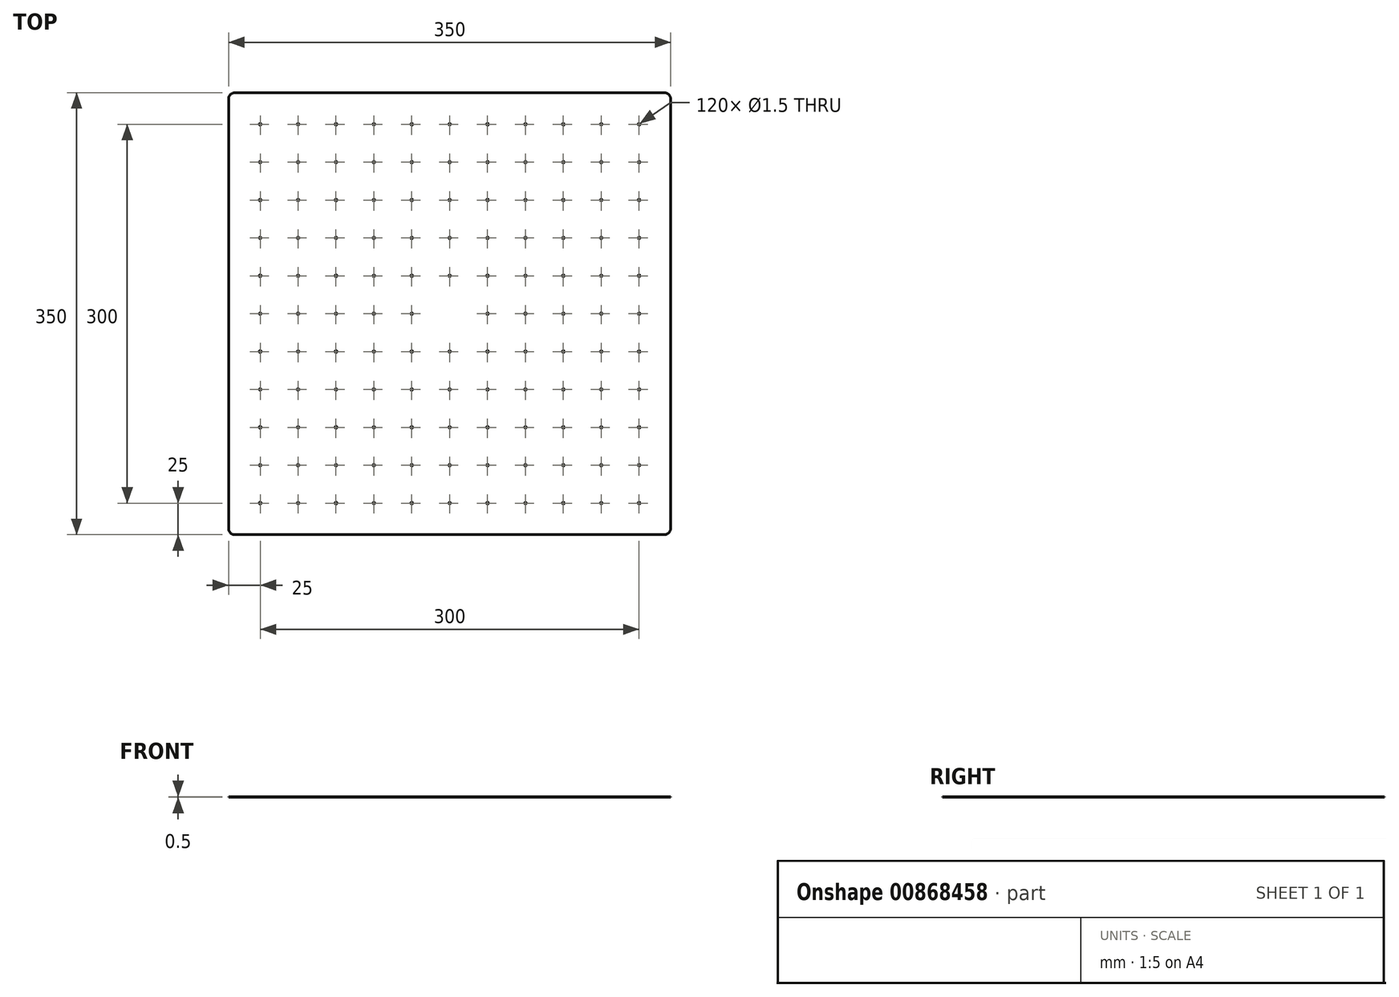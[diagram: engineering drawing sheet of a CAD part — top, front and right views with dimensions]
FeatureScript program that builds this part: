
annotation { "Feature Type Name" : "Feature", "Feature Type Description" : "" }
export const myFeature = defineFeature(function(context is Context, id is Id, definition is map)
    precondition{}
    {
        {
            var Q0;
            Q0=qCreatedBy(makeId("Top.planeOp"),FACE);
            var sketch = newSketch(context, id + "F0", { "sketchPlane" : qUnion([Q0])});
            skLineSegment(sketch, "E0.bottom", {"start": v(-170, -175) * mm, "end": v(170, -175) * mm});
            skLineSegment(sketch, "E0.top", {"start": v(-170, 175) * mm, "end": v(170, 175) * mm});
            skLineSegment(sketch, "E0.left", {"start": v(-175, -170) * mm, "end": v(-175, 170) * mm});
            skLineSegment(sketch, "E0.right", {"start": v(175, -170) * mm, "end": v(175, 170) * mm});
            skPoint(sketch, "E0.middle", {"position": v(0, 0) * mm});
            skPoint(sketch, "E1.visualSharp", {"position": v(-175, 175) * mm});
            skArc(sketch, "E1.filletArc", {"start": v(-170, 175) * mm, "mid": v(-173.54, 173.54) * mm, "end": v(-175, 170) * mm});
            skPoint(sketch, "E2.visualSharp", {"position": v(175, 175) * mm});
            skArc(sketch, "E2.filletArc", {"start": v(175, 170) * mm, "mid": v(173.54, 173.54) * mm, "end": v(170, 175) * mm});
            skPoint(sketch, "E3.visualSharp", {"position": v(175, -175) * mm});
            skArc(sketch, "E3.filletArc", {"start": v(170, -175) * mm, "mid": v(173.54, -173.54) * mm, "end": v(175, -170) * mm});
            skPoint(sketch, "E4.visualSharp", {"position": v(-175, -175) * mm});
            skArc(sketch, "E4.filletArc", {"start": v(-175, -170) * mm, "mid": v(-173.54, -173.54) * mm, "end": v(-170, -175) * mm});
            skCircle(sketch, "E5", {"center": v(-150, 150) * mm, "radius": 0.75 * mm});
            skCircle(sketch, "E6.0.1.0", {"center": v(-150, 120) * mm, "radius": 0.75 * mm});
            skCircle(sketch, "E6.0.2.0", {"center": v(-150, 90) * mm, "radius": 0.75 * mm});
            skCircle(sketch, "E6.0.3.0", {"center": v(-150, 60) * mm, "radius": 0.75 * mm});
            skCircle(sketch, "E6.0.4.0", {"center": v(-150, 30) * mm, "radius": 0.75 * mm});
            skCircle(sketch, "E6.0.5.0", {"center": v(-150, 0) * mm, "radius": 0.75 * mm});
            skCircle(sketch, "E6.0.6.0", {"center": v(-150, -30) * mm, "radius": 0.75 * mm});
            skCircle(sketch, "E6.0.7.0", {"center": v(-150, -60) * mm, "radius": 0.75 * mm});
            skCircle(sketch, "E6.0.8.0", {"center": v(-150, -90) * mm, "radius": 0.75 * mm});
            skCircle(sketch, "E6.0.9.0", {"center": v(-150, -120) * mm, "radius": 0.75 * mm});
            skCircle(sketch, "E6.0.10.0", {"center": v(-150, -150) * mm, "radius": 0.75 * mm});
            skCircle(sketch, "E6.1.0.0", {"center": v(-120, 150) * mm, "radius": 0.75 * mm});
            skCircle(sketch, "E6.1.1.0", {"center": v(-120, 120) * mm, "radius": 0.75 * mm});
            skCircle(sketch, "E6.1.2.0", {"center": v(-120, 90) * mm, "radius": 0.75 * mm});
            skCircle(sketch, "E6.1.3.0", {"center": v(-120, 60) * mm, "radius": 0.75 * mm});
            skCircle(sketch, "E6.1.4.0", {"center": v(-120, 30) * mm, "radius": 0.75 * mm});
            skCircle(sketch, "E6.1.5.0", {"center": v(-120, 0) * mm, "radius": 0.75 * mm});
            skCircle(sketch, "E6.1.6.0", {"center": v(-120, -30) * mm, "radius": 0.75 * mm});
            skCircle(sketch, "E6.1.7.0", {"center": v(-120, -60) * mm, "radius": 0.75 * mm});
            skCircle(sketch, "E6.1.8.0", {"center": v(-120, -90) * mm, "radius": 0.75 * mm});
            skCircle(sketch, "E6.1.9.0", {"center": v(-120, -120) * mm, "radius": 0.75 * mm});
            skCircle(sketch, "E6.1.10.0", {"center": v(-120, -150) * mm, "radius": 0.75 * mm});
            skCircle(sketch, "E6.2.0.0", {"center": v(-90, 150) * mm, "radius": 0.75 * mm});
            skCircle(sketch, "E6.2.1.0", {"center": v(-90, 120) * mm, "radius": 0.75 * mm});
            skCircle(sketch, "E6.2.2.0", {"center": v(-90, 90) * mm, "radius": 0.75 * mm});
            skCircle(sketch, "E6.2.3.0", {"center": v(-90, 60) * mm, "radius": 0.75 * mm});
            skCircle(sketch, "E6.2.4.0", {"center": v(-90, 30) * mm, "radius": 0.75 * mm});
            skCircle(sketch, "E6.2.5.0", {"center": v(-90, 0) * mm, "radius": 0.75 * mm});
            skCircle(sketch, "E6.2.6.0", {"center": v(-90, -30) * mm, "radius": 0.75 * mm});
            skCircle(sketch, "E6.2.7.0", {"center": v(-90, -60) * mm, "radius": 0.75 * mm});
            skCircle(sketch, "E6.2.8.0", {"center": v(-90, -90) * mm, "radius": 0.75 * mm});
            skCircle(sketch, "E6.2.9.0", {"center": v(-90, -120) * mm, "radius": 0.75 * mm});
            skCircle(sketch, "E6.2.10.0", {"center": v(-90, -150) * mm, "radius": 0.75 * mm});
            skCircle(sketch, "E6.3.0.0", {"center": v(-60, 150) * mm, "radius": 0.75 * mm});
            skCircle(sketch, "E6.3.1.0", {"center": v(-60, 120) * mm, "radius": 0.75 * mm});
            skCircle(sketch, "E6.3.2.0", {"center": v(-60, 90) * mm, "radius": 0.75 * mm});
            skCircle(sketch, "E6.3.3.0", {"center": v(-60, 60) * mm, "radius": 0.75 * mm});
            skCircle(sketch, "E6.3.4.0", {"center": v(-60, 30) * mm, "radius": 0.75 * mm});
            skCircle(sketch, "E6.3.5.0", {"center": v(-60, 0) * mm, "radius": 0.75 * mm});
            skCircle(sketch, "E6.3.6.0", {"center": v(-60, -30) * mm, "radius": 0.75 * mm});
            skCircle(sketch, "E6.3.7.0", {"center": v(-60, -60) * mm, "radius": 0.75 * mm});
            skCircle(sketch, "E6.3.8.0", {"center": v(-60, -90) * mm, "radius": 0.75 * mm});
            skCircle(sketch, "E6.3.9.0", {"center": v(-60, -120) * mm, "radius": 0.75 * mm});
            skCircle(sketch, "E6.3.10.0", {"center": v(-60, -150) * mm, "radius": 0.75 * mm});
            skCircle(sketch, "E6.4.0.0", {"center": v(-30, 150) * mm, "radius": 0.75 * mm});
            skCircle(sketch, "E6.4.1.0", {"center": v(-30, 120) * mm, "radius": 0.75 * mm});
            skCircle(sketch, "E6.4.2.0", {"center": v(-30, 90) * mm, "radius": 0.75 * mm});
            skCircle(sketch, "E6.4.3.0", {"center": v(-30, 60) * mm, "radius": 0.75 * mm});
            skCircle(sketch, "E6.4.4.0", {"center": v(-30, 30) * mm, "radius": 0.75 * mm});
            skCircle(sketch, "E6.4.5.0", {"center": v(-30, 0) * mm, "radius": 0.75 * mm});
            skCircle(sketch, "E6.4.6.0", {"center": v(-30, -30) * mm, "radius": 0.75 * mm});
            skCircle(sketch, "E6.4.7.0", {"center": v(-30, -60) * mm, "radius": 0.75 * mm});
            skCircle(sketch, "E6.4.8.0", {"center": v(-30, -90) * mm, "radius": 0.75 * mm});
            skCircle(sketch, "E6.4.9.0", {"center": v(-30, -120) * mm, "radius": 0.75 * mm});
            skCircle(sketch, "E6.4.10.0", {"center": v(-30, -150) * mm, "radius": 0.75 * mm});
            skCircle(sketch, "E6.5.0.0", {"center": v(0, 150) * mm, "radius": 0.75 * mm});
            skCircle(sketch, "E6.5.1.0", {"center": v(0, 120) * mm, "radius": 0.75 * mm});
            skCircle(sketch, "E6.5.2.0", {"center": v(0, 90) * mm, "radius": 0.75 * mm});
            skCircle(sketch, "E6.5.3.0", {"center": v(0, 60) * mm, "radius": 0.75 * mm});
            skCircle(sketch, "E6.5.4.0", {"center": v(0, 30) * mm, "radius": 0.75 * mm});
            skCircle(sketch, "E6.5.5.0", {"center": v(0, 0) * mm, "radius": 0.75 * mm});
            skCircle(sketch, "E6.5.6.0", {"center": v(0, -30) * mm, "radius": 0.75 * mm});
            skCircle(sketch, "E6.5.7.0", {"center": v(0, -60) * mm, "radius": 0.75 * mm});
            skCircle(sketch, "E6.5.8.0", {"center": v(0, -90) * mm, "radius": 0.75 * mm});
            skCircle(sketch, "E6.5.9.0", {"center": v(0, -120) * mm, "radius": 0.75 * mm});
            skCircle(sketch, "E6.5.10.0", {"center": v(0, -150) * mm, "radius": 0.75 * mm});
            skCircle(sketch, "E6.6.0.0", {"center": v(30, 150) * mm, "radius": 0.75 * mm});
            skCircle(sketch, "E6.6.1.0", {"center": v(30, 120) * mm, "radius": 0.75 * mm});
            skCircle(sketch, "E6.6.2.0", {"center": v(30, 90) * mm, "radius": 0.75 * mm});
            skCircle(sketch, "E6.6.3.0", {"center": v(30, 60) * mm, "radius": 0.75 * mm});
            skCircle(sketch, "E6.6.4.0", {"center": v(30, 30) * mm, "radius": 0.75 * mm});
            skCircle(sketch, "E6.6.5.0", {"center": v(30, 0) * mm, "radius": 0.75 * mm});
            skCircle(sketch, "E6.6.6.0", {"center": v(30, -30) * mm, "radius": 0.75 * mm});
            skCircle(sketch, "E6.6.7.0", {"center": v(30, -60) * mm, "radius": 0.75 * mm});
            skCircle(sketch, "E6.6.8.0", {"center": v(30, -90) * mm, "radius": 0.75 * mm});
            skCircle(sketch, "E6.6.9.0", {"center": v(30, -120) * mm, "radius": 0.75 * mm});
            skCircle(sketch, "E6.6.10.0", {"center": v(30, -150) * mm, "radius": 0.75 * mm});
            skCircle(sketch, "E6.7.0.0", {"center": v(60, 150) * mm, "radius": 0.75 * mm});
            skCircle(sketch, "E6.7.1.0", {"center": v(60, 120) * mm, "radius": 0.75 * mm});
            skCircle(sketch, "E6.7.2.0", {"center": v(60, 90) * mm, "radius": 0.75 * mm});
            skCircle(sketch, "E6.7.3.0", {"center": v(60, 60) * mm, "radius": 0.75 * mm});
            skCircle(sketch, "E6.7.4.0", {"center": v(60, 30) * mm, "radius": 0.75 * mm});
            skCircle(sketch, "E6.7.5.0", {"center": v(60, 0) * mm, "radius": 0.75 * mm});
            skCircle(sketch, "E6.7.6.0", {"center": v(60, -30) * mm, "radius": 0.75 * mm});
            skCircle(sketch, "E6.7.7.0", {"center": v(60, -60) * mm, "radius": 0.75 * mm});
            skCircle(sketch, "E6.7.8.0", {"center": v(60, -90) * mm, "radius": 0.75 * mm});
            skCircle(sketch, "E6.7.9.0", {"center": v(60, -120) * mm, "radius": 0.75 * mm});
            skCircle(sketch, "E6.7.10.0", {"center": v(60, -150) * mm, "radius": 0.75 * mm});
            skCircle(sketch, "E6.8.0.0", {"center": v(90, 150) * mm, "radius": 0.75 * mm});
            skCircle(sketch, "E6.8.1.0", {"center": v(90, 120) * mm, "radius": 0.75 * mm});
            skCircle(sketch, "E6.8.2.0", {"center": v(90, 90) * mm, "radius": 0.75 * mm});
            skCircle(sketch, "E6.8.3.0", {"center": v(90, 60) * mm, "radius": 0.75 * mm});
            skCircle(sketch, "E6.8.4.0", {"center": v(90, 30) * mm, "radius": 0.75 * mm});
            skCircle(sketch, "E6.8.5.0", {"center": v(90, 0) * mm, "radius": 0.75 * mm});
            skCircle(sketch, "E6.8.6.0", {"center": v(90, -30) * mm, "radius": 0.75 * mm});
            skCircle(sketch, "E6.8.7.0", {"center": v(90, -60) * mm, "radius": 0.75 * mm});
            skCircle(sketch, "E6.8.8.0", {"center": v(90, -90) * mm, "radius": 0.75 * mm});
            skCircle(sketch, "E6.8.9.0", {"center": v(90, -120) * mm, "radius": 0.75 * mm});
            skCircle(sketch, "E6.8.10.0", {"center": v(90, -150) * mm, "radius": 0.75 * mm});
            skCircle(sketch, "E6.9.0.0", {"center": v(120, 150) * mm, "radius": 0.75 * mm});
            skCircle(sketch, "E6.9.1.0", {"center": v(120, 120) * mm, "radius": 0.75 * mm});
            skCircle(sketch, "E6.9.2.0", {"center": v(120, 90) * mm, "radius": 0.75 * mm});
            skCircle(sketch, "E6.9.3.0", {"center": v(120, 60) * mm, "radius": 0.75 * mm});
            skCircle(sketch, "E6.9.4.0", {"center": v(120, 30) * mm, "radius": 0.75 * mm});
            skCircle(sketch, "E6.9.5.0", {"center": v(120, 0) * mm, "radius": 0.75 * mm});
            skCircle(sketch, "E6.9.6.0", {"center": v(120, -30) * mm, "radius": 0.75 * mm});
            skCircle(sketch, "E6.9.7.0", {"center": v(120, -60) * mm, "radius": 0.75 * mm});
            skCircle(sketch, "E6.9.8.0", {"center": v(120, -90) * mm, "radius": 0.75 * mm});
            skCircle(sketch, "E6.9.9.0", {"center": v(120, -120) * mm, "radius": 0.75 * mm});
            skCircle(sketch, "E6.9.10.0", {"center": v(120, -150) * mm, "radius": 0.75 * mm});
            skCircle(sketch, "E6.10.0.0", {"center": v(150, 150) * mm, "radius": 0.75 * mm});
            skCircle(sketch, "E6.10.1.0", {"center": v(150, 120) * mm, "radius": 0.75 * mm});
            skCircle(sketch, "E6.10.2.0", {"center": v(150, 90) * mm, "radius": 0.75 * mm});
            skCircle(sketch, "E6.10.3.0", {"center": v(150, 60) * mm, "radius": 0.75 * mm});
            skCircle(sketch, "E6.10.4.0", {"center": v(150, 30) * mm, "radius": 0.75 * mm});
            skCircle(sketch, "E6.10.5.0", {"center": v(150, 0) * mm, "radius": 0.75 * mm});
            skCircle(sketch, "E6.10.6.0", {"center": v(150, -30) * mm, "radius": 0.75 * mm});
            skCircle(sketch, "E6.10.7.0", {"center": v(150, -60) * mm, "radius": 0.75 * mm});
            skCircle(sketch, "E6.10.8.0", {"center": v(150, -90) * mm, "radius": 0.75 * mm});
            skCircle(sketch, "E6.10.9.0", {"center": v(150, -120) * mm, "radius": 0.75 * mm});
            skCircle(sketch, "E6.10.10.0", {"center": v(150, -150) * mm, "radius": 0.75 * mm});
            skLineSegment(sketch, "E6.direction1", {"start": v(-150, 150) * mm, "end": v(-120, 150) * mm, "construction": true});
            skLineSegment(sketch, "E6.direction2", {"start": v(-150, 150) * mm, "end": v(-150, 120) * mm, "construction": true});
            skSolve(sketch);
        }
        {
            var Q0;
            Q0 = qSketchRegion(id + "F0", true);
            extrude(context, id + "F1", {"entities" : qUnion([Q0]), "depth" : 0.5 * mm, "offsetDistance" : 25 * mm});
        }
        {
            var Q0;
            Q0=makeQuery(id+"F1.opExtrude","CAP_FACE",FACE,{"disambiguationData":[OSD([sQuery(id+"F0.wireOp",EDGE,"E0.bottom"),sQuery(id+"F0.wireOp",EDGE,"E0.top"),sQuery(id+"F0.wireOp",EDGE,"E0.left"),sQuery(id+"F0.wireOp",EDGE,"E0.right"),sQuery(id+"F0.wireOp",EDGE,"E1.filletArc"),sQuery(id+"F0.wireOp",EDGE,"E2.filletArc"),sQuery(id+"F0.wireOp",EDGE,"E3.filletArc"),sQuery(id+"F0.wireOp",EDGE,"E4.filletArc"),sQuery(id+"F0.wireOp",EDGE,"E5"),sQuery(id+"F0.wireOp",EDGE,"E6.0.1.0"),sQuery(id+"F0.wireOp",EDGE,"E6.0.2.0"),sQuery(id+"F0.wireOp",EDGE,"E6.0.3.0"),sQuery(id+"F0.wireOp",EDGE,"E6.0.4.0"),sQuery(id+"F0.wireOp",EDGE,"E6.0.5.0"),sQuery(id+"F0.wireOp",EDGE,"E6.0.6.0"),sQuery(id+"F0.wireOp",EDGE,"E6.0.7.0"),sQuery(id+"F0.wireOp",EDGE,"E6.0.8.0"),sQuery(id+"F0.wireOp",EDGE,"E6.0.9.0"),sQuery(id+"F0.wireOp",EDGE,"E6.0.10.0"),sQuery(id+"F0.wireOp",EDGE,"E6.1.0.0"),sQuery(id+"F0.wireOp",EDGE,"E6.1.1.0"),sQuery(id+"F0.wireOp",EDGE,"E6.1.2.0"),sQuery(id+"F0.wireOp",EDGE,"E6.1.3.0"),sQuery(id+"F0.wireOp",EDGE,"E6.1.4.0"),sQuery(id+"F0.wireOp",EDGE,"E6.1.5.0"),sQuery(id+"F0.wireOp",EDGE,"E6.1.6.0"),sQuery(id+"F0.wireOp",EDGE,"E6.1.7.0"),sQuery(id+"F0.wireOp",EDGE,"E6.1.8.0"),sQuery(id+"F0.wireOp",EDGE,"E6.1.9.0"),sQuery(id+"F0.wireOp",EDGE,"E6.1.10.0"),sQuery(id+"F0.wireOp",EDGE,"E6.2.0.0"),sQuery(id+"F0.wireOp",EDGE,"E6.2.1.0"),sQuery(id+"F0.wireOp",EDGE,"E6.2.2.0"),sQuery(id+"F0.wireOp",EDGE,"E6.2.3.0"),sQuery(id+"F0.wireOp",EDGE,"E6.2.4.0"),sQuery(id+"F0.wireOp",EDGE,"E6.2.5.0"),sQuery(id+"F0.wireOp",EDGE,"E6.2.6.0"),sQuery(id+"F0.wireOp",EDGE,"E6.2.7.0"),sQuery(id+"F0.wireOp",EDGE,"E6.2.8.0"),sQuery(id+"F0.wireOp",EDGE,"E6.2.9.0"),sQuery(id+"F0.wireOp",EDGE,"E6.2.10.0"),sQuery(id+"F0.wireOp",EDGE,"E6.3.0.0"),sQuery(id+"F0.wireOp",EDGE,"E6.3.1.0"),sQuery(id+"F0.wireOp",EDGE,"E6.3.2.0"),sQuery(id+"F0.wireOp",EDGE,"E6.3.3.0"),sQuery(id+"F0.wireOp",EDGE,"E6.3.4.0"),sQuery(id+"F0.wireOp",EDGE,"E6.3.5.0"),sQuery(id+"F0.wireOp",EDGE,"E6.3.6.0"),sQuery(id+"F0.wireOp",EDGE,"E6.3.7.0"),sQuery(id+"F0.wireOp",EDGE,"E6.3.8.0"),sQuery(id+"F0.wireOp",EDGE,"E6.3.9.0"),sQuery(id+"F0.wireOp",EDGE,"E6.3.10.0"),sQuery(id+"F0.wireOp",EDGE,"E6.4.0.0"),sQuery(id+"F0.wireOp",EDGE,"E6.4.1.0"),sQuery(id+"F0.wireOp",EDGE,"E6.4.2.0"),sQuery(id+"F0.wireOp",EDGE,"E6.4.3.0"),sQuery(id+"F0.wireOp",EDGE,"E6.4.4.0"),sQuery(id+"F0.wireOp",EDGE,"E6.4.5.0"),sQuery(id+"F0.wireOp",EDGE,"E6.4.6.0"),sQuery(id+"F0.wireOp",EDGE,"E6.4.7.0"),sQuery(id+"F0.wireOp",EDGE,"E6.4.8.0"),sQuery(id+"F0.wireOp",EDGE,"E6.4.9.0"),sQuery(id+"F0.wireOp",EDGE,"E6.4.10.0"),sQuery(id+"F0.wireOp",EDGE,"E6.5.0.0"),sQuery(id+"F0.wireOp",EDGE,"E6.5.1.0"),sQuery(id+"F0.wireOp",EDGE,"E6.5.2.0"),sQuery(id+"F0.wireOp",EDGE,"E6.5.3.0"),sQuery(id+"F0.wireOp",EDGE,"E6.5.4.0"),sQuery(id+"F0.wireOp",EDGE,"E6.5.5.0"),sQuery(id+"F0.wireOp",EDGE,"E6.5.6.0"),sQuery(id+"F0.wireOp",EDGE,"E6.5.7.0"),sQuery(id+"F0.wireOp",EDGE,"E6.5.8.0"),sQuery(id+"F0.wireOp",EDGE,"E6.5.9.0"),sQuery(id+"F0.wireOp",EDGE,"E6.5.10.0"),sQuery(id+"F0.wireOp",EDGE,"E6.6.0.0"),sQuery(id+"F0.wireOp",EDGE,"E6.6.1.0"),sQuery(id+"F0.wireOp",EDGE,"E6.6.2.0"),sQuery(id+"F0.wireOp",EDGE,"E6.6.3.0"),sQuery(id+"F0.wireOp",EDGE,"E6.6.4.0"),sQuery(id+"F0.wireOp",EDGE,"E6.6.5.0"),sQuery(id+"F0.wireOp",EDGE,"E6.6.6.0"),sQuery(id+"F0.wireOp",EDGE,"E6.6.7.0"),sQuery(id+"F0.wireOp",EDGE,"E6.6.8.0"),sQuery(id+"F0.wireOp",EDGE,"E6.6.9.0"),sQuery(id+"F0.wireOp",EDGE,"E6.6.10.0"),sQuery(id+"F0.wireOp",EDGE,"E6.7.0.0"),sQuery(id+"F0.wireOp",EDGE,"E6.7.1.0"),sQuery(id+"F0.wireOp",EDGE,"E6.7.2.0"),sQuery(id+"F0.wireOp",EDGE,"E6.7.3.0"),sQuery(id+"F0.wireOp",EDGE,"E6.7.4.0"),sQuery(id+"F0.wireOp",EDGE,"E6.7.5.0"),sQuery(id+"F0.wireOp",EDGE,"E6.7.6.0"),sQuery(id+"F0.wireOp",EDGE,"E6.7.7.0"),sQuery(id+"F0.wireOp",EDGE,"E6.7.8.0"),sQuery(id+"F0.wireOp",EDGE,"E6.7.9.0"),sQuery(id+"F0.wireOp",EDGE,"E6.7.10.0"),sQuery(id+"F0.wireOp",EDGE,"E6.8.0.0"),sQuery(id+"F0.wireOp",EDGE,"E6.8.1.0"),sQuery(id+"F0.wireOp",EDGE,"E6.8.2.0"),sQuery(id+"F0.wireOp",EDGE,"E6.8.3.0"),sQuery(id+"F0.wireOp",EDGE,"E6.8.4.0"),sQuery(id+"F0.wireOp",EDGE,"E6.8.5.0"),sQuery(id+"F0.wireOp",EDGE,"E6.8.6.0"),sQuery(id+"F0.wireOp",EDGE,"E6.8.7.0"),sQuery(id+"F0.wireOp",EDGE,"E6.8.8.0"),sQuery(id+"F0.wireOp",EDGE,"E6.8.9.0"),sQuery(id+"F0.wireOp",EDGE,"E6.8.10.0"),sQuery(id+"F0.wireOp",EDGE,"E6.9.0.0"),sQuery(id+"F0.wireOp",EDGE,"E6.9.1.0"),sQuery(id+"F0.wireOp",EDGE,"E6.9.2.0"),sQuery(id+"F0.wireOp",EDGE,"E6.9.3.0"),sQuery(id+"F0.wireOp",EDGE,"E6.9.4.0"),sQuery(id+"F0.wireOp",EDGE,"E6.9.5.0"),sQuery(id+"F0.wireOp",EDGE,"E6.9.6.0"),sQuery(id+"F0.wireOp",EDGE,"E6.9.7.0"),sQuery(id+"F0.wireOp",EDGE,"E6.9.8.0"),sQuery(id+"F0.wireOp",EDGE,"E6.9.9.0"),sQuery(id+"F0.wireOp",EDGE,"E6.9.10.0"),sQuery(id+"F0.wireOp",EDGE,"E6.10.0.0"),sQuery(id+"F0.wireOp",EDGE,"E6.10.1.0"),sQuery(id+"F0.wireOp",EDGE,"E6.10.2.0"),sQuery(id+"F0.wireOp",EDGE,"E6.10.3.0"),sQuery(id+"F0.wireOp",EDGE,"E6.10.4.0"),sQuery(id+"F0.wireOp",EDGE,"E6.10.5.0"),sQuery(id+"F0.wireOp",EDGE,"E6.10.6.0"),sQuery(id+"F0.wireOp",EDGE,"E6.10.7.0"),sQuery(id+"F0.wireOp",EDGE,"E6.10.8.0"),sQuery(id+"F0.wireOp",EDGE,"E6.10.9.0"),sQuery(id+"F0.wireOp",EDGE,"E6.10.10.0")])],"isStart":true});
            var sketch = newSketch(context, id + "F2", { "sketchPlane" : qUnion([Q0])});
            skLineSegment(sketch, "E7.bottom", {"start": v(1.54, 1.52) * mm, "end": v(-5.54, 1.52) * mm});
            skLineSegment(sketch, "E7.top", {"start": v(1.54, -5.51) * mm, "end": v(-5.54, -5.51) * mm});
            skLineSegment(sketch, "E7.left", {"start": v(1.54, 1.52) * mm, "end": v(1.54, -5.51) * mm});
            skLineSegment(sketch, "E7.right", {"start": v(-5.54, 1.52) * mm, "end": v(-5.54, -5.51) * mm});
            skPoint(sketch, "E7.middle", {"position": v(-2, -2) * mm});
            skSolve(sketch);
        }
        {
            var Q0;
            Q0 = qSketchRegion(id + "F2", true);
            extrude(context, id + "F3", {"entities" : qUnion([Q0]), "operationType" : NewBodyOperationType.ADD, "oppositeDirection" : true, "depth" : 0.5 * mm, "offsetDistance" : 25 * mm});
        }
    });
